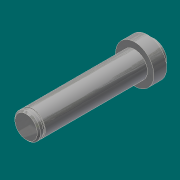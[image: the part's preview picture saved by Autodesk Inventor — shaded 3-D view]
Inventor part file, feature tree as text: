
AUTODESK INVENTOR PART (.ipt)
format: ipt  version: 2017 (Build 210142000, 142)  size: 109,056 bytes
history: native  units: in
note: dims shown in document units (in); Inventor stores cm internally (conversion verified against a paired STEP export)
features: extrude x5, sketch x5, chamfer x1
ambient origin geometry x8: Origin, YZ Plane, XZ Plane, XY Plane, X Axis, Y Axis, Z Axis, Center Point
bodies: Solid1 (feature_tree)
feature tree (11):
  extrude  "Extrusion1"  Depth=0.25in TaperAngle=0.0deg
  extrude  "Extrusion2"  Depth=2.0in TaperAngle=0.0deg
  extrude  "Extrusion3"  Depth=0.04in TaperAngle=0.0deg
  extrude  "Extrusion4"  Depth=0.125in TaperAngle=45.0deg
  chamfer  "Chamfer1"  Distance=0.125in
  extrude  "Extrusion5"  [1 undecoded]
  sketch  "Sketch1"  dims[d0=0.75in d1=0.25in d2=0.0in]
  sketch  "Sketch2"  dims[d3=0.5in d4=2.0in d5=0.0in]
  sketch  "Sketch3"  dims[d6=0.4688in d7=0.04in d8=0.0in]
  sketch  "Sketch4"  dims[d9=0.085in d10=0.0in d11=0.0312in d12=0.125in d13=45.0deg]
  sketch  "Sketch5"  dims[d14=0.5in d15=0.125in d16=0.0in]
note: 1 required parameter value undecoded (feature->parameter linkage not recoverable at this tier; creation-order binding heuristic only, values carry confidence <= 0.55)
